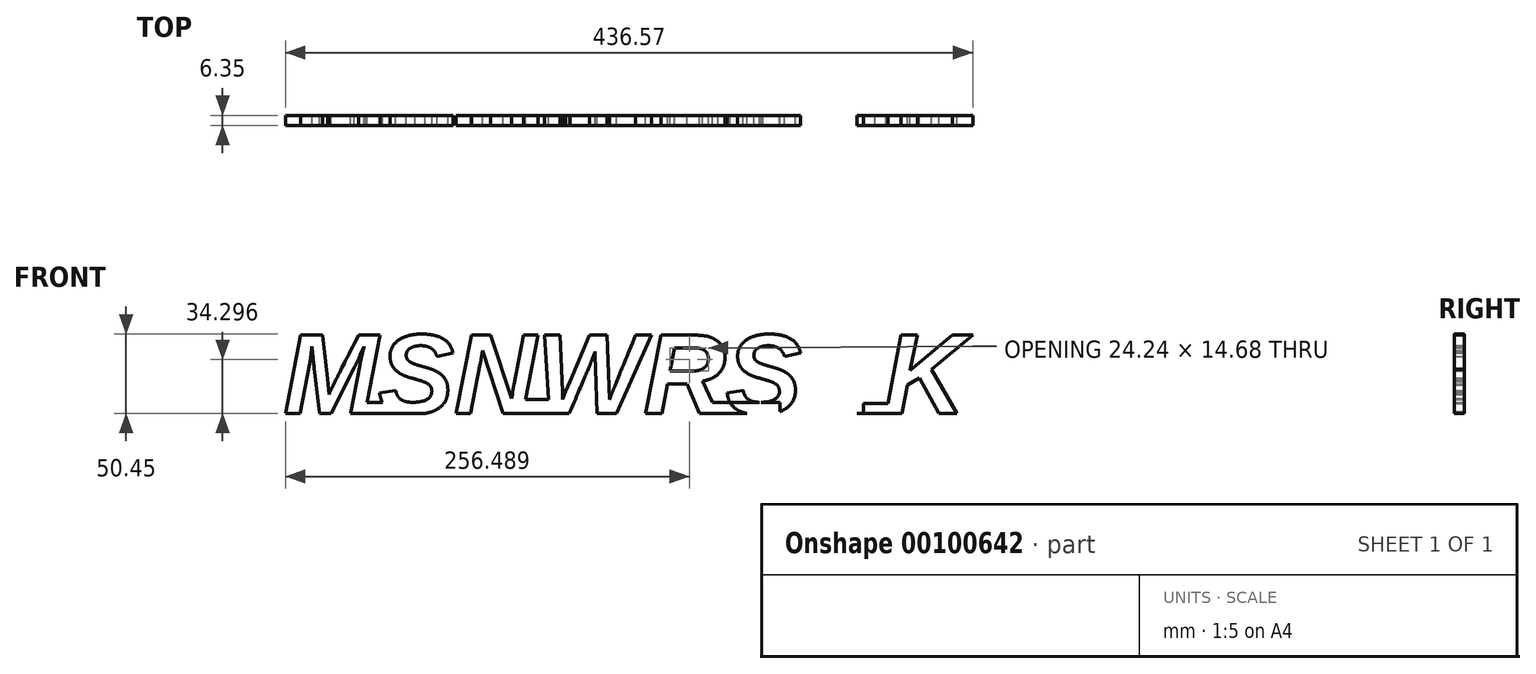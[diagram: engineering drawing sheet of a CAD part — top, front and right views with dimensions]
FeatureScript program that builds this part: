
annotation { "Feature Type Name" : "Feature", "Feature Type Description" : "" }
export const myFeature = defineFeature(function(context is Context, id is Id, definition is map)
    precondition{}
    {
        {
            var Q0;
            Q0=qCreatedBy(makeId("Front.planeOp"),FACE);
            var sketch = newSketch(context, id + "F0", { "sketchPlane" : qUnion([Q0])});
            skText(sketch, "E0", { "text": "MSNWRSKK", "fontName": "Arimo-BoldItalic.ttf"});
            skLineSegment(sketch, "E1", {"start": v(-188.06, 0.18) * mm, "end": v(-149.57, 0.18) * mm});
            skLineSegment(sketch, "E2", {"start": v(-154.27, 7.29) * mm, "end": v(-188.06, 7.29) * mm});
            skLineSegment(sketch, "E3", {"start": v(-188.06, 7.29) * mm, "end": v(-188.06, 0.18) * mm});
            skLineSegment(sketch, "E4", {"start": v(-154.27, 7.29) * mm, "end": v(-154.27, 0) * mm});
            skLineSegment(sketch, "E5.top", {"start": v(-39.48, 0.18) * mm, "end": v(-71.85, 0.18) * mm});
            skLineSegment(sketch, "E6.bottom", {"start": v(72.43, 0.18) * mm, "end": v(106.05, 0.18) * mm});
            skLineSegment(sketch, "E7", {"start": v(-149.57, 0.18) * mm, "end": v(-144.35, 0.18) * mm});
            skLineSegment(sketch, "E8", {"start": v(106.05, 0.18) * mm, "end": v(131.48, 0.18) * mm});
            skLineSegment(sketch, "E9.bottom", {"start": v(-91.48, 0.18) * mm, "end": v(-60.03, 0.18) * mm});
            skLineSegment(sketch, "E9.top", {"start": v(-91.48, 8.96) * mm, "end": v(-60.03, 8.96) * mm});
            skLineSegment(sketch, "E9.left", {"start": v(-91.48, 0.18) * mm, "end": v(-91.48, 8.96) * mm});
            skLineSegment(sketch, "E9.right", {"start": v(-60.03, 0.18) * mm, "end": v(-60.03, 8.96) * mm});
            skLineSegment(sketch, "E10.bottom", {"start": v(33.7, 0.18) * mm, "end": v(78.53, 0.18) * mm});
            skLineSegment(sketch, "E10.top", {"start": v(33.7, 7.27) * mm, "end": v(78.53, 7.27) * mm});
            skLineSegment(sketch, "E10.left", {"start": v(33.7, 0.18) * mm, "end": v(33.7, 7.27) * mm});
            skLineSegment(sketch, "E10.right", {"start": v(78.53, 0.18) * mm, "end": v(78.53, 7.27) * mm});
            skLineSegment(sketch, "E11.bottom", {"start": v(131.48, 0.18) * mm, "end": v(152.44, 0.18) * mm});
            skLineSegment(sketch, "E11.top", {"start": v(131.48, 6.53) * mm, "end": v(152.44, 6.53) * mm});
            skLineSegment(sketch, "E11.left", {"start": v(131.48, 0.18) * mm, "end": v(131.48, 6.53) * mm});
            skLineSegment(sketch, "E11.right", {"start": v(152.44, 0.18) * mm, "end": v(152.44, 6.53) * mm});
            const initialGuessF0  = {"E0": [-0.23682, 0.00018, 1, 0, 0.05202]};
            skSetInitialGuess(sketch, initialGuessF0);
            skSolve(sketch);
        }
        {
            var Q0;
            {var subQ0=sQuery(id+"F0.wireOp",EDGE,"E6.bottom");var subQ1=sQuery(id+"F0.wireOp",EDGE,"E0.sketch_text.stroke-93");var subQ2=makeQuery(id+"F0.imprint","INTERSECT",VERTEX,{"derivedFrom":[subQ1,subQ0]});Q0=makeQuery(id+"F0.imprint","IMPRINT",FACE,{"disambiguationData":[TD([[makeQuery(id+"F0.imprint","IMPRINT",EDGE,{"disambiguationData":[TD([[subQ2,1.0]])],"derivedFrom":subQ1}),1.0]])]});}
            var Q1;
            Q1=makeQuery(id+"F0.imprint","IMPRINT",FACE,{"disambiguationData":[TD([[makeQuery(id+"F0.imprint","IMPRINT",EDGE,{"derivedFrom":sQuery(id+"F0.wireOp",EDGE,"E0.sketch_text.stroke-131")}),-1.0]])]});
            var Q2;
            Q2=makeQuery(id+"F0.imprint","IMPRINT",FACE,{"disambiguationData":[TD([[makeQuery(id+"F0.imprint","IMPRINT",EDGE,{"derivedFrom":sQuery(id+"F0.wireOp",EDGE,"E0.sketch_text.stroke-0")}),-1.0]])]});
            var Q3;
            {var subQ5=sQuery(id+"F0.wireOp",EDGE,"E3");Q3=makeQuery(id+"F0.imprint","IMPRINT",FACE,{"disambiguationData":[TD([[makeQuery(id+"F0.imprint","IMPRINT",EDGE,{"derivedFrom":subQ5}),1.0]])]});}
            var Q4;
            {var subQ0=sQuery(id+"F0.wireOp",EDGE,"E1");var subQ1=sQuery(id+"F0.wireOp",EDGE,"E0.sketch_text.stroke-18");var subQ2=makeQuery(id+"F0.imprint","INTERSECT",VERTEX,{"derivedFrom":[subQ1,subQ0]});Q4=makeQuery(id+"F0.imprint","IMPRINT",FACE,{"disambiguationData":[TD([[makeQuery(id+"F0.imprint","IMPRINT",EDGE,{"disambiguationData":[TD([[subQ2,1.0]])],"derivedFrom":subQ1}),1.0]])]});}
            var Q5;
            {var subQ5=sQuery(id+"F0.wireOp",EDGE,"E0.sketch_text.stroke-21");var subQ6=sQuery(id+"F0.wireOp",EDGE,"E0.sketch_text.stroke-20");var subQ7=makeQuery(id+"F0.imprint","INTERSECT",VERTEX,{"derivedFrom":[subQ6,subQ5]});Q5=makeQuery(id+"F0.imprint","IMPRINT",FACE,{"disambiguationData":[TD([[makeQuery(id+"F0.imprint","IMPRINT",EDGE,{"disambiguationData":[TD([[subQ7,1.0]])],"derivedFrom":subQ6}),-1.0]])]});}
            var Q6;
            {var subQ4=sQuery(id+"F0.wireOp",EDGE,"E0.sketch_text.stroke-22");Q6=makeQuery(id+"F0.imprint","IMPRINT",FACE,{"disambiguationData":[TD([[makeQuery(id+"F0.imprint","IMPRINT",EDGE,{"derivedFrom":subQ4}),-1.0]])]});}
            var Q7;
            {var subQ4=sQuery(id+"F0.wireOp",EDGE,"E0.sketch_text.stroke-26");Q7=makeQuery(id+"F0.imprint","IMPRINT",FACE,{"disambiguationData":[TD([[makeQuery(id+"F0.imprint","IMPRINT",EDGE,{"derivedFrom":subQ4}),-1.0]])]});}
            var Q8;
            Q8=makeQuery(id+"F0.imprint","IMPRINT",FACE,{"disambiguationData":[TD([[makeQuery(id+"F0.imprint","IMPRINT",EDGE,{"derivedFrom":sQuery(id+"F0.wireOp",EDGE,"E0.sketch_text.stroke-49")}),-1.0]])]});
            var Q9;
            {var subQ5=sQuery(id+"F0.wireOp",EDGE,"E5.right");Q9=makeQuery(id+"F0.imprint","IMPRINT",FACE,{"disambiguationData":[TD([[makeQuery(id+"F0.imprint","IMPRINT",EDGE,{"derivedFrom":subQ5}),1.0]])]});}
            var Q10;
            {var subQ0=sQuery(id+"F0.wireOp",EDGE,"E5.top");var subQ1=sQuery(id+"F0.wireOp",EDGE,"E0.sketch_text.stroke-60");var subQ2=makeQuery(id+"F0.imprint","INTERSECT",VERTEX,{"derivedFrom":[subQ1,subQ0]});Q10=makeQuery(id+"F0.imprint","IMPRINT",FACE,{"disambiguationData":[TD([[makeQuery(id+"F0.imprint","IMPRINT",EDGE,{"disambiguationData":[TD([[subQ2,1.0]])],"derivedFrom":subQ1}),1.0]])]});}
            var Q11;
            {var subQ1=sQuery(id+"F0.wireOp",EDGE,"E0.sketch_text.stroke-69");var subQ9=sQuery(id+"F0.wireOp",EDGE,"E5.top");var subQ11=makeQuery(id+"F0.imprint","INTERSECT",VERTEX,{"derivedFrom":[subQ1,subQ9]});Q11=makeQuery(id+"F0.imprint","IMPRINT",FACE,{"disambiguationData":[TD([[makeQuery(id+"F0.imprint","IMPRINT",EDGE,{"disambiguationData":[TD([[subQ11,-1.0]])],"derivedFrom":subQ1}),-1.0]])]});}
            var Q12;
            {var subQ4=sQuery(id+"F0.wireOp",EDGE,"E0.sketch_text.stroke-70");Q12=makeQuery(id+"F0.imprint","IMPRINT",FACE,{"disambiguationData":[TD([[makeQuery(id+"F0.imprint","IMPRINT",EDGE,{"derivedFrom":subQ4}),-1.0]])]});}
            var Q13;
            Q13=makeQuery(id+"F0.imprint","IMPRINT",FACE,{"disambiguationData":[TD([[makeQuery(id+"F0.imprint","IMPRINT",EDGE,{"derivedFrom":sQuery(id+"F0.wireOp",EDGE,"E0.sketch_text.stroke-62")}),-1.0]])]});
            var Q14;
            Q14=makeQuery(id+"F0.imprint","IMPRINT",FACE,{"disambiguationData":[TD([[makeQuery(id+"F0.imprint","IMPRINT",EDGE,{"derivedFrom":sQuery(id+"F0.wireOp",EDGE,"E0.sketch_text.stroke-82")}),-1.0]])]});
            var Q15;
            {var subQ5=sQuery(id+"F0.wireOp",EDGE,"E6.left");Q15=makeQuery(id+"F0.imprint","IMPRINT",FACE,{"disambiguationData":[TD([[makeQuery(id+"F0.imprint","IMPRINT",EDGE,{"derivedFrom":subQ5}),-1.0]])]});}
            var Q16;
            {var subQ5=sQuery(id+"F0.wireOp",EDGE,"E0.sketch_text.stroke-104");Q16=makeQuery(id+"F0.imprint","IMPRINT",FACE,{"disambiguationData":[TD([[makeQuery(id+"F0.imprint","IMPRINT",EDGE,{"derivedFrom":subQ5}),-1.0]])]});}
            var Q17;
            {var subQ0=sQuery(id+"F0.wireOp",EDGE,"E6.right");Q17=makeQuery(id+"F0.imprint","IMPRINT",FACE,{"disambiguationData":[TD([[makeQuery(id+"F0.imprint","IMPRINT",EDGE,{"derivedFrom":subQ0}),1.0]])]});}
            var Q18;
            {var subQ5=sQuery(id+"F0.wireOp",EDGE,"wRV7HIRr-suSL-cWsi-kY2I-ZdENqN4VlPPJ.left");Q18=makeQuery(id+"F0.imprint","IMPRINT",FACE,{"disambiguationData":[TD([[makeQuery(id+"F0.imprint","IMPRINT",EDGE,{"derivedFrom":subQ5}),-1.0]])]});}
            var Q19;
            {var subQ0=sQuery(id+"F0.wireOp",EDGE,"wRV7HIRr-suSL-cWsi-kY2I-ZdENqN4VlPPJ.bottom");var subQ1=sQuery(id+"F0.wireOp",EDGE,"E0.sketch_text.stroke-141");var subQ2=makeQuery(id+"F0.imprint","INTERSECT",VERTEX,{"derivedFrom":[subQ1,subQ0]});Q19=makeQuery(id+"F0.imprint","IMPRINT",FACE,{"disambiguationData":[TD([[makeQuery(id+"F0.imprint","IMPRINT",EDGE,{"disambiguationData":[TD([[subQ2,1.0]])],"derivedFrom":subQ1}),1.0]])]});}
            var Q20;
            {var subQ5=sQuery(id+"F0.wireOp",EDGE,"wRV7HIRr-suSL-cWsi-kY2I-ZdENqN4VlPPJ.bottom");var subQ6=sQuery(id+"F0.wireOp",EDGE,"E0.sketch_text.stroke-145");var subQ7=makeQuery(id+"F0.imprint","INTERSECT",VERTEX,{"derivedFrom":[subQ6,subQ5]});Q20=makeQuery(id+"F0.imprint","IMPRINT",FACE,{"disambiguationData":[TD([[makeQuery(id+"F0.imprint","IMPRINT",EDGE,{"disambiguationData":[TD([[subQ7,1.0]])],"derivedFrom":subQ6}),-1.0]])]});}
            var Q21;
            Q21=makeQuery(id+"F0.imprint","IMPRINT",FACE,{"disambiguationData":[TD([[makeQuery(id+"F0.imprint","IMPRINT",EDGE,{"derivedFrom":sQuery(id+"F0.wireOp",EDGE,"E0.sketch_text.stroke-143")}),-1.0]])]});
            var Q22;
            {var subQ5=sQuery(id+"F0.wireOp",EDGE,"E9.left");Q22=makeQuery(id+"F0.imprint","IMPRINT",FACE,{"disambiguationData":[TD([[makeQuery(id+"F0.imprint","IMPRINT",EDGE,{"derivedFrom":subQ5}),-1.0]])]});}
            var Q23;
            {var subQ8=sQuery(id+"F0.wireOp",EDGE,"E10.bottom");var subQ10=makeQuery(id+"F0.imprint","IMPRINT",VERTEX,{"derivedFrom":subQ8});Q23=makeQuery(id+"F0.imprint","IMPRINT",FACE,{"disambiguationData":[TD([[makeQuery(id+"F0.imprint","IMPRINT",EDGE,{"disambiguationData":[TD([[subQ10,1.0]])],"derivedFrom":subQ8}),1.0]])]});}
            var Q24;
            {var subQ5=sQuery(id+"F0.wireOp",EDGE,"E10.left");Q24=makeQuery(id+"F0.imprint","IMPRINT",FACE,{"disambiguationData":[TD([[makeQuery(id+"F0.imprint","IMPRINT",EDGE,{"derivedFrom":subQ5}),-1.0]])]});}
            var Q25;
            {var subQ4=sQuery(id+"F0.wireOp",EDGE,"E0.sketch_text.stroke-108");Q25=makeQuery(id+"F0.imprint","IMPRINT",FACE,{"disambiguationData":[TD([[makeQuery(id+"F0.imprint","IMPRINT",EDGE,{"derivedFrom":subQ4}),-1.0]])]});}
            var Q26;
            {var subQ5=sQuery(id+"F0.wireOp",EDGE,"E11.left");Q26=makeQuery(id+"F0.imprint","IMPRINT",FACE,{"disambiguationData":[TD([[makeQuery(id+"F0.imprint","IMPRINT",EDGE,{"derivedFrom":subQ5}),-1.0]])]});}
            var Q27;
            {var subQ5=sQuery(id+"F0.wireOp",EDGE,"E11.right");Q27=makeQuery(id+"F0.imprint","IMPRINT",FACE,{"disambiguationData":[TD([[makeQuery(id+"F0.imprint","IMPRINT",EDGE,{"derivedFrom":subQ5}),1.0]])]});}
            extrude(context, id + "F1", {"entities" : qUnion([Q0, Q1, Q2, Q3, Q4, Q5, Q6, Q7, Q8, Q9, Q10, Q11, Q12, Q13, Q14, Q15, Q16, Q17, Q18, Q19, Q20, Q21, Q22, Q23, Q24, Q25, Q26, Q27]), "depth" : 6.35 * mm});
        }
    });
